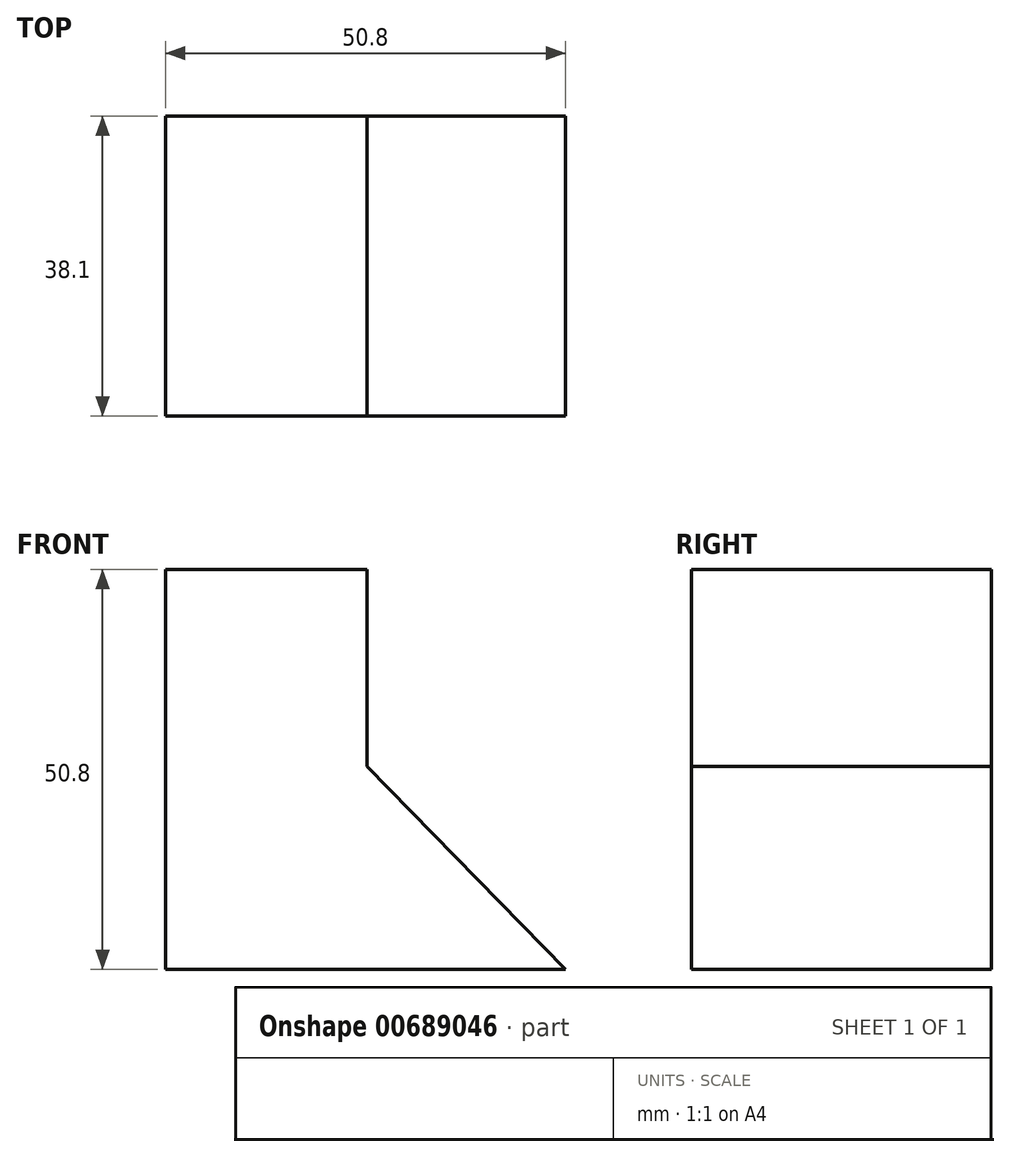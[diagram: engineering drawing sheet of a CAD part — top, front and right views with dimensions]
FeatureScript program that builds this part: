
annotation { "Feature Type Name" : "Feature", "Feature Type Description" : "" }
export const myFeature = defineFeature(function(context is Context, id is Id, definition is map)
    precondition{}
    {
        {
            var Q0;
            Q0=qCreatedBy(makeId("Front.planeOp"),FACE);
            var sketch = newSketch(context, id + "F0", { "sketchPlane" : qUnion([Q0])});
            skLineSegment(sketch, "E0", {"start": v(0, 0) * mm, "end": v(-50.8, 0) * mm});
            skLineSegment(sketch, "E1", {"start": v(-50.8, 0) * mm, "end": v(-50.8, 50.8) * mm});
            skLineSegment(sketch, "E2", {"start": v(-50.8, 50.8) * mm, "end": v(-25.18, 50.8) * mm});
            skLineSegment(sketch, "E3", {"start": v(-25.18, 50.8) * mm, "end": v(-25.18, 25.76) * mm});
            skLineSegment(sketch, "E4", {"start": v(-25.18, 25.76) * mm, "end": v(0, 0) * mm});
            skSolve(sketch);
        }
        {
            var Q0;
            Q0=makeQuery(id+"F0.imprint","IMPRINT",FACE,{"disambiguationData":[TD([[makeQuery(id+"F0.imprint","IMPRINT",EDGE,{"derivedFrom":sQuery(id+"F0.wireOp",EDGE,"E0")}),-1.0]])]});
            extrude(context, id + "F1", {"entities" : qUnion([Q0]), "depth" : 38.1 * mm, "offsetDistance" : 25.4 * mm});
        }
    });
